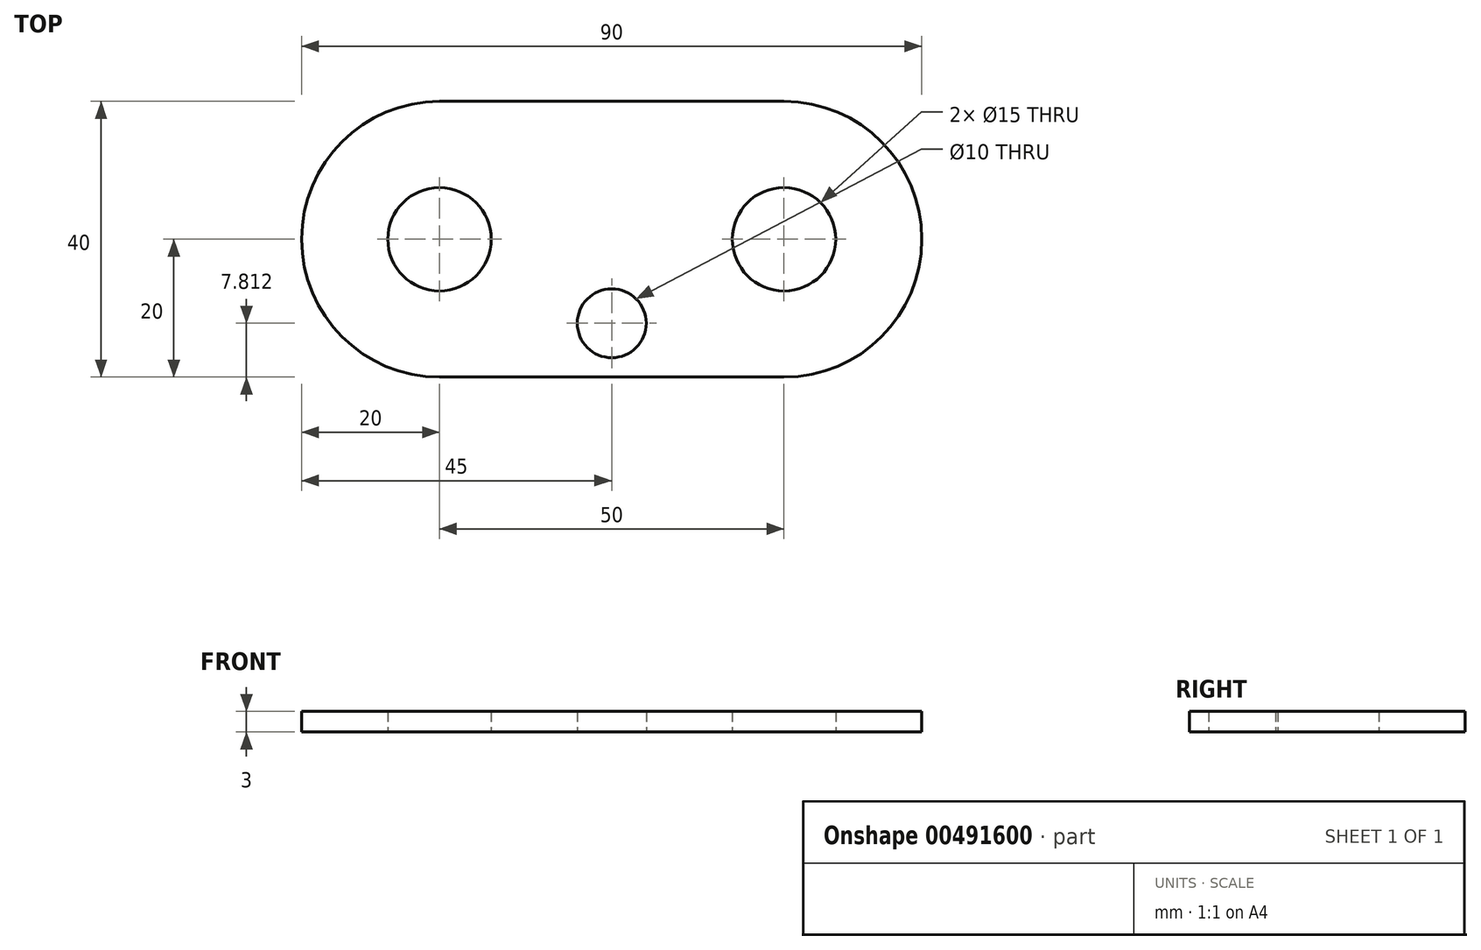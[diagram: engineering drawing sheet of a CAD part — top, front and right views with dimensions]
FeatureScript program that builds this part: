
annotation { "Feature Type Name" : "Feature", "Feature Type Description" : "" }
export const myFeature = defineFeature(function(context is Context, id is Id, definition is map)
    precondition{}
    {
        {
            var Q0;
            Q0=qCreatedBy(makeId("Top.planeOp"),FACE);
            var sketch = newSketch(context, id + "F0", { "sketchPlane" : qUnion([Q0])});
            skCircle(sketch, "E0", {"center": v(0, 0) * mm, "radius": 20 * mm});
            skLineSegment(sketch, "E1.bottom", {"start": v(0, -20) * mm, "end": v(50, -20) * mm});
            skLineSegment(sketch, "E1.top", {"start": v(0, 20) * mm, "end": v(50, 20) * mm});
            skLineSegment(sketch, "E1.left", {"start": v(0, -20) * mm, "end": v(0, 20) * mm});
            skLineSegment(sketch, "E1.right", {"start": v(50, -20) * mm, "end": v(50, 20) * mm});
            skCircle(sketch, "E2", {"center": v(50, 0) * mm, "radius": 20 * mm});
            skCircle(sketch, "E3", {"center": v(0, 0) * mm, "radius": 7.5 * mm});
            skCircle(sketch, "E4", {"center": v(50, 0) * mm, "radius": 7.5 * mm});
            skCircle(sketch, "E5", {"center": v(25, -12.19) * mm, "radius": 7.81 * mm});
            skLineSegment(sketch, "E6", {"start": v(25, -12.19) * mm, "end": v(32.02, -8.76) * mm, "construction": true});
            skLineSegment(sketch, "E7", {"start": v(25, -12.19) * mm, "end": v(17.98, -8.76) * mm, "construction": true});
            skLineSegment(sketch, "E8", {"start": v(25, -12.19) * mm, "end": v(25, -20) * mm, "construction": true});
            skCircle(sketch, "E9", {"center": v(25, -12.19) * mm, "radius": 5 * mm});
            skSolve(sketch);
        }
        {
            var Q0;
            {var subQ0=sQuery(id+"F0.wireOp",EDGE,"E1.left");var subQ3=sQuery(id+"F0.wireOp",EDGE,"E3");var subQ7=makeQuery(id+"F0.imprint","INTERSECT",VERTEX,{"disambiguationData":[OD(0.0)],"derivedFrom":[subQ0,subQ3]});Q0=makeQuery(id+"F0.imprint","IMPRINT",FACE,{"disambiguationData":[TD([[makeQuery(id+"F0.imprint","IMPRINT",EDGE,{"disambiguationData":[TD([[subQ7,-1.0]])],"derivedFrom":subQ3}),-1.0]])]});}
            var Q1;
            {var subQ0=sQuery(id+"F0.wireOp",EDGE,"E1.left");var subQ4=sQuery(id+"F0.wireOp",EDGE,"E3");var subQ5=makeQuery(id+"F0.imprint","INTERSECT",VERTEX,{"disambiguationData":[OD(0.0)],"derivedFrom":[subQ0,subQ4]});Q1=makeQuery(id+"F0.imprint","IMPRINT",FACE,{"disambiguationData":[TD([[makeQuery(id+"F0.imprint","IMPRINT",EDGE,{"disambiguationData":[TD([[subQ5,1.0]])],"derivedFrom":subQ4}),-1.0]])]});}
            var Q2;
            {var subQ0=sQuery(id+"F0.wireOp",EDGE,"E1.top");Q2=makeQuery(id+"F0.imprint","IMPRINT",FACE,{"disambiguationData":[TD([[makeQuery(id+"F0.imprint","IMPRINT",EDGE,{"derivedFrom":subQ0}),-1.0]])]});}
            var Q3;
            {var subQ0=sQuery(id+"F0.wireOp",EDGE,"E1.bottom");var subQ3=sQuery(id+"F0.wireOp",EDGE,"E5");var subQ5=makeQuery(id+"F0.imprint","INTERSECT",VERTEX,{"derivedFrom":[subQ0,subQ3]});Q3=makeQuery(id+"F0.imprint","IMPRINT",FACE,{"disambiguationData":[TD([[makeQuery(id+"F0.imprint","IMPRINT",EDGE,{"disambiguationData":[TD([[subQ5,1.0]])],"derivedFrom":subQ3}),-1.0]])]});}
            var Q4;
            Q4=makeQuery(id+"F0.imprint","IMPRINT",FACE,{"disambiguationData":[TD([[makeQuery(id+"F0.imprint","IMPRINT",EDGE,{"derivedFrom":sQuery(id+"F0.wireOp",EDGE,"E9")}),-1.0]])]});
            var Q5;
            {var subQ1=sQuery(id+"F0.wireOp",EDGE,"E1.bottom");var subQ3=sQuery(id+"F0.wireOp",EDGE,"E5");var subQ4=makeQuery(id+"F0.imprint","INTERSECT",VERTEX,{"derivedFrom":[subQ1,subQ3]});Q5=makeQuery(id+"F0.imprint","IMPRINT",FACE,{"disambiguationData":[TD([[makeQuery(id+"F0.imprint","IMPRINT",EDGE,{"disambiguationData":[TD([[subQ4,-1.0]])],"derivedFrom":subQ3}),-1.0]])]});}
            var Q6;
            {var subQ1=sQuery(id+"F0.wireOp",EDGE,"E1.right");var subQ5=sQuery(id+"F0.wireOp",EDGE,"E4");var subQ7=makeQuery(id+"F0.imprint","INTERSECT",VERTEX,{"disambiguationData":[OD(0.0)],"derivedFrom":[subQ1,subQ5]});Q6=makeQuery(id+"F0.imprint","IMPRINT",FACE,{"disambiguationData":[TD([[makeQuery(id+"F0.imprint","IMPRINT",EDGE,{"disambiguationData":[TD([[subQ7,1.0]])],"derivedFrom":subQ5}),-1.0]])]});}
            var Q7;
            {var subQ1=sQuery(id+"F0.wireOp",EDGE,"E1.right");var subQ3=sQuery(id+"F0.wireOp",EDGE,"E4");var subQ4=makeQuery(id+"F0.imprint","INTERSECT",VERTEX,{"disambiguationData":[OD(0.0)],"derivedFrom":[subQ1,subQ3]});Q7=makeQuery(id+"F0.imprint","IMPRINT",FACE,{"disambiguationData":[TD([[makeQuery(id+"F0.imprint","IMPRINT",EDGE,{"disambiguationData":[TD([[subQ4,-1.0]])],"derivedFrom":subQ3}),-1.0]])]});}
            extrude(context, id + "F1", {"entities" : qUnion([Q0, Q1, Q2, Q3, Q4, Q5, Q6, Q7]), "depth" : 3 * mm});
        }
    });
